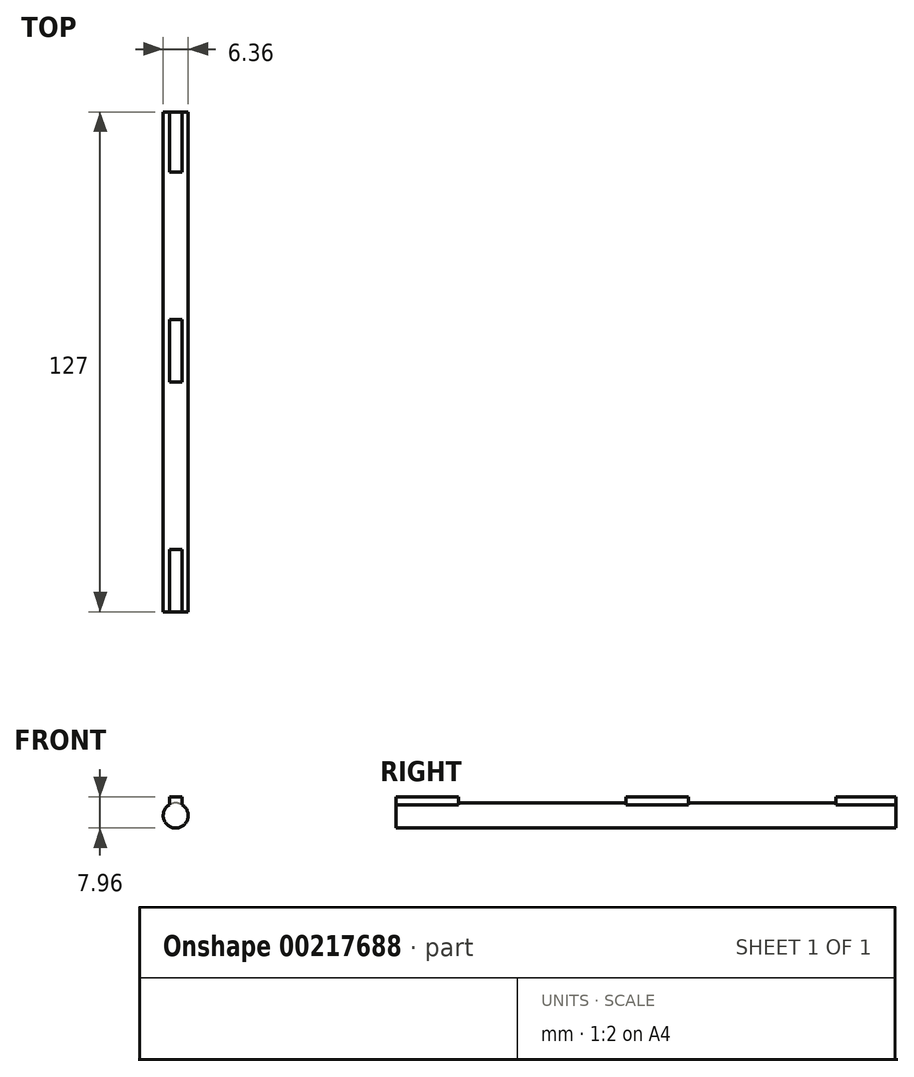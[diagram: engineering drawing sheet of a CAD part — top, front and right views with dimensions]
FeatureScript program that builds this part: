
annotation { "Feature Type Name" : "Feature", "Feature Type Description" : "" }
export const myFeature = defineFeature(function(context is Context, id is Id, definition is map)
    precondition{}
    {
        {
            var Q0;
            Q0=qCreatedBy(makeId("Front.planeOp"),FACE);
            var sketch = newSketch(context, id + "F0", { "sketchPlane" : qUnion([Q0])});
            skCircle(sketch, "E0", {"center": v(0, 0) * mm, "radius": 3.18 * mm});
            skSolve(sketch);
        }
        {
            var Q0;
            Q0 = qSketchRegion(id + "F0", true);
            extrude(context, id + "F1", {"entities" : qUnion([Q0]), "depth" : 127 * mm});
        }
        {
            var Q0;
            Q0=makeQuery(id+"F1.opExtrude","CAP_FACE",FACE,{"disambiguationData":[OSD([sQuery(id+"F0.wireOp",EDGE,"E0")])],"isStart":false});
            var sketch = newSketch(context, id + "F2", { "sketchPlane" : qUnion([Q0])});
            skLineSegment(sketch, "E1.bottom", {"start": v(-1.59, 1.6) * mm, "end": v(1.59, 1.6) * mm});
            skLineSegment(sketch, "E1.top", {"start": v(-1.59, 4.78) * mm, "end": v(1.59, 4.78) * mm});
            skLineSegment(sketch, "E1.left", {"start": v(-1.59, 1.6) * mm, "end": v(-1.59, 4.78) * mm});
            skLineSegment(sketch, "E1.right", {"start": v(1.59, 1.6) * mm, "end": v(1.59, 4.78) * mm});
            skLineSegment(sketch, "E2", {"start": v(0, 1.6) * mm, "end": v(0, 4.78) * mm});
            skSolve(sketch);
        }
        {
            var Q0;
            Q0 = qSketchRegion(id + "F2", true);
            extrude(context, id + "F3", {"entities" : qUnion([Q0]), "operationType" : NewBodyOperationType.ADD, "oppositeDirection" : true, "depth" : 15.88 * mm});
        }
        {
            var Q0;
            Q0=makeQuery(id+"F3.boolean.opBoolean","MERGE",FACE,{"derivedFrom":[makeQuery(id+"F1.opExtrude","CAP_FACE",FACE,{"disambiguationData":[OSD([sQuery(id+"F0.wireOp",EDGE,"E0")])],"isStart":false}),makeQuery(id+"F3.opExtrude","CAP_FACE",FACE,{"disambiguationData":[OSD([sQuery(id+"F2.wireOp",EDGE,"E1.bottom"),sQuery(id+"F2.wireOp",EDGE,"E1.top"),sQuery(id+"F2.wireOp",EDGE,"E1.left"),sQuery(id+"F2.wireOp",EDGE,"E1.right")])],"isStart":true})]});
            cPlane(context, id + "F4", {"entities" : qUnion([Q0]), "cplaneType" : CPlaneType.OFFSET, "offset" : 58.42 * mm, "oppositeDirection" : true, "width" : 152.4 * mm, "height" : 152.4 * mm});
        }
        {
            var Q0;
            Q0=qCreatedBy(id+"F4.planeOp",FACE);
            var sketch = newSketch(context, id + "F5", { "sketchPlane" : qUnion([Q0])});
            skLineSegment(sketch, "E3.bottom", {"start": v(-1.59, 1.6) * mm, "end": v(1.59, 1.6) * mm});
            skLineSegment(sketch, "E3.top", {"start": v(-1.59, 4.78) * mm, "end": v(1.59, 4.78) * mm});
            skLineSegment(sketch, "E3.left", {"start": v(-1.59, 1.6) * mm, "end": v(-1.59, 4.78) * mm});
            skLineSegment(sketch, "E3.right", {"start": v(1.59, 1.6) * mm, "end": v(1.59, 4.78) * mm});
            skSolve(sketch);
        }
        {
            var Q0;
            Q0 = qSketchRegion(id + "F5", true);
            extrude(context, id + "F6", {"entities" : qUnion([Q0]), "operationType" : NewBodyOperationType.ADD, "oppositeDirection" : true, "depth" : 15.88 * mm});
        }
        {
            var Q0;
            Q0=makeQuery(id+"F3.boolean.opBoolean","MERGE",FACE,{"derivedFrom":[makeQuery(id+"F1.opExtrude","CAP_FACE",FACE,{"disambiguationData":[OSD([sQuery(id+"F0.wireOp",EDGE,"E0")])],"isStart":false}),makeQuery(id+"F3.opExtrude","CAP_FACE",FACE,{"disambiguationData":[OSD([sQuery(id+"F2.wireOp",EDGE,"E1.bottom"),sQuery(id+"F2.wireOp",EDGE,"E1.top"),sQuery(id+"F2.wireOp",EDGE,"E1.left"),sQuery(id+"F2.wireOp",EDGE,"E1.right")])],"isStart":true})]});
            cPlane(context, id + "F7", {"entities" : qUnion([Q0]), "cplaneType" : CPlaneType.OFFSET, "offset" : 111.76 * mm, "oppositeDirection" : true, "width" : 152.4 * mm, "height" : 152.4 * mm});
        }
        {
            var Q0;
            Q0=qCreatedBy(id+"F7.planeOp",FACE);
            var sketch = newSketch(context, id + "F8", { "sketchPlane" : qUnion([Q0])});
            skLineSegment(sketch, "E4.bottom", {"start": v(-1.59, 1.66) * mm, "end": v(1.59, 1.66) * mm});
            skLineSegment(sketch, "E4.top", {"start": v(-1.59, 4.78) * mm, "end": v(1.59, 4.78) * mm});
            skLineSegment(sketch, "E4.left", {"start": v(-1.59, 1.66) * mm, "end": v(-1.59, 4.78) * mm});
            skLineSegment(sketch, "E4.right", {"start": v(1.59, 1.66) * mm, "end": v(1.59, 4.78) * mm});
            skSolve(sketch);
        }
        {
            var Q0;
            Q0 = qSketchRegion(id + "F8", true);
            extrude(context, id + "F9", {"entities" : qUnion([Q0]), "operationType" : NewBodyOperationType.ADD, "oppositeDirection" : true, "depth" : 15.24 * mm});
        }
    });
